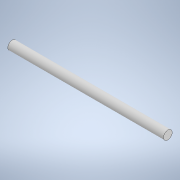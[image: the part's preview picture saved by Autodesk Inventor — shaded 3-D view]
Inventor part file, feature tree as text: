
AUTODESK INVENTOR PART (.ipt)
format: ipt  version: 2021 (Build 250183000, 183)  size: 91,648 bytes
history: native  units: in
note: dims shown in document units (in); Inventor stores cm internally (conversion verified against a paired STEP export)
features: extrude x1, sketch x1
ambient origin geometry x8: Origin, YZ Plane, XZ Plane, XY Plane, X Axis, Y Axis, Z Axis, Center Point
bodies: Solid1 (feature_tree)
feature tree (2):
  extrude  "Extrusion1"  Depth=4.5in TaperAngle=0.0deg
  sketch  "Sketch1"  dims[d0=0.25in d1=4.5in d2=0.0in]
